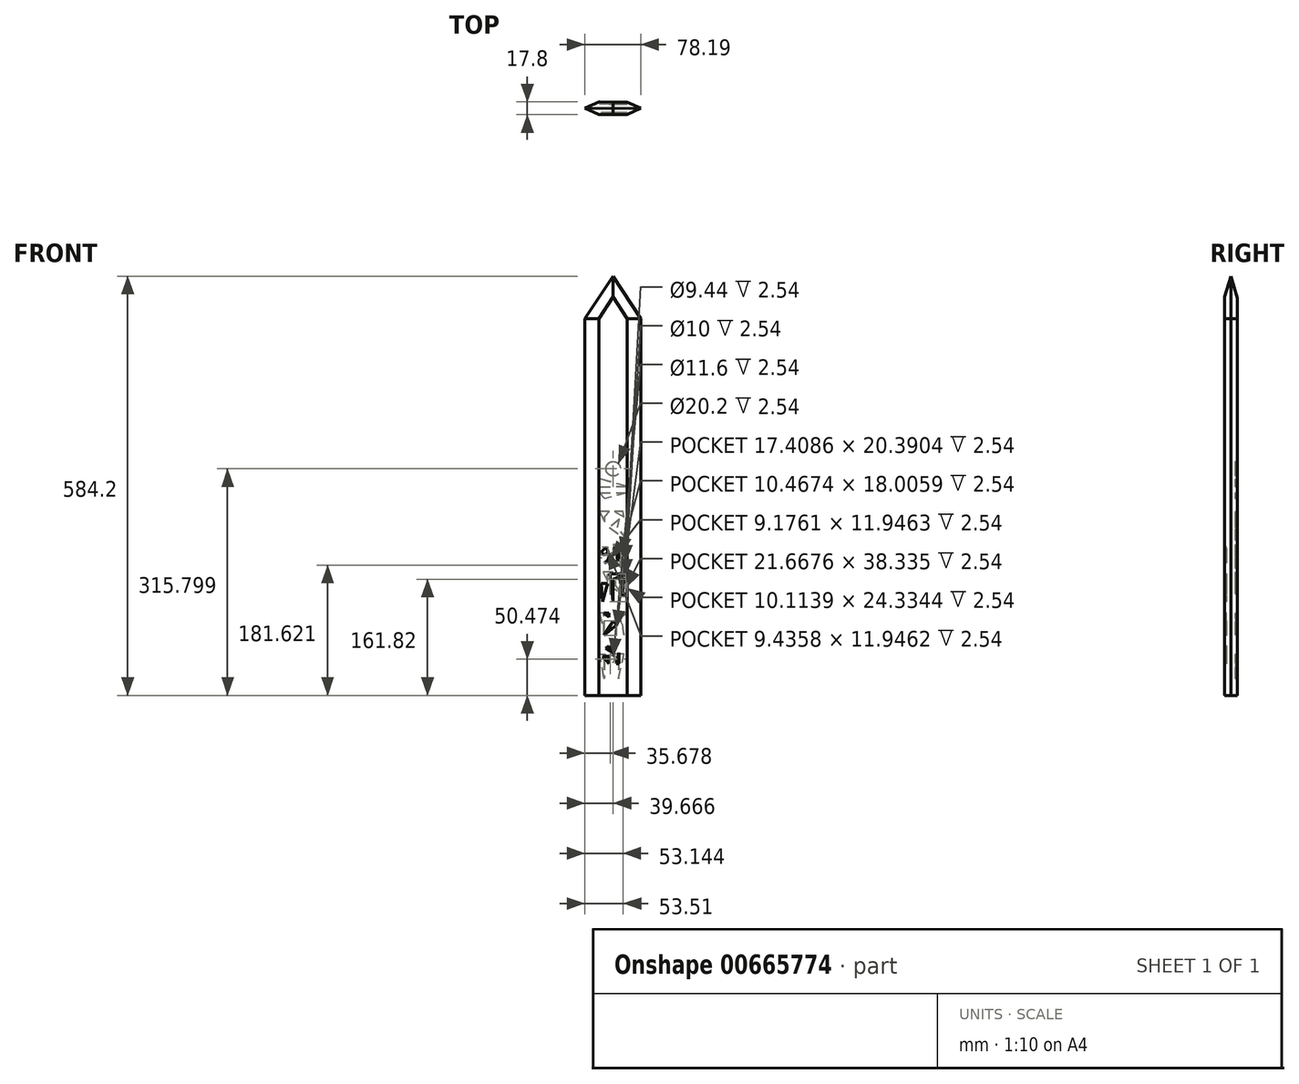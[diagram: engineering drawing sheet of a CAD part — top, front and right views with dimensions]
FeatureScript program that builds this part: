
annotation { "Feature Type Name" : "Feature", "Feature Type Description" : "" }
export const myFeature = defineFeature(function(context is Context, id is Id, definition is map)
    precondition{}
    {
        {
            var Q0;
            Q0=qCreatedBy(makeId("Top.planeOp"),FACE);
            var sketch = newSketch(context, id + "F0", { "sketchPlane" : qUnion([Q0])});
            skLineSegment(sketch, "E0.bottom", {"start": v(-40.34, -18.56) * mm, "end": v(39.23, -18.56) * mm});
            skLineSegment(sketch, "E0.top", {"start": v(-40.34, 17.67) * mm, "end": v(39.23, 17.67) * mm});
            skLineSegment(sketch, "E0.left", {"start": v(-40.34, -18.56) * mm, "end": v(-40.34, 17.67) * mm});
            skLineSegment(sketch, "E0.right", {"start": v(39.23, -18.56) * mm, "end": v(39.23, 17.67) * mm});
            skSolve(sketch);
        }
        {
            var Q0;
            Q0=makeQuery(id+"F0.imprint","IMPRINT",FACE,{"disambiguationData":[TD([[makeQuery(id+"F0.imprint","IMPRINT",EDGE,{"derivedFrom":sQuery(id+"F0.wireOp",EDGE,"E0.bottom")}),1.0]])]});
            extrude(context, id + "F1", {"entities" : qUnion([Q0]), "depth" : 12.7 * mm, "offsetDistance" : 25.4 * mm});
        }
        {
            var Q0;
            Q0=makeQuery(id+"F1.opExtrude","CAP_FACE",FACE,{"disambiguationData":[OSD([sQuery(id+"F0.wireOp",EDGE,"E0.bottom"),sQuery(id+"F0.wireOp",EDGE,"E0.top"),sQuery(id+"F0.wireOp",EDGE,"E0.left"),sQuery(id+"F0.wireOp",EDGE,"E0.right")])],"isStart":true});
            extrude(context, id + "F2", {"entities" : qUnion([Q0]), "operationType" : NewBodyOperationType.ADD, "depth" : 12.7 * mm, "offsetDistance" : 25.4 * mm});
        }
        {
            var Q0;
            Q0=makeQuery(id+"F1.opExtrude","CAP_FACE",FACE,{"disambiguationData":[OSD([sQuery(id+"F0.wireOp",EDGE,"E0.bottom"),sQuery(id+"F0.wireOp",EDGE,"E0.top"),sQuery(id+"F0.wireOp",EDGE,"E0.left"),sQuery(id+"F0.wireOp",EDGE,"E0.right")])],"isStart":false});
            var sketch = newSketch(context, id + "F3", { "sketchPlane" : qUnion([Q0])});
            skLineSegment(sketch, "E1", {"start": v(0, -17.92) * mm, "end": v(-39.6, 0) * mm});
            skLineSegment(sketch, "E2", {"start": v(0, -17.92) * mm, "end": v(38.59, 0) * mm});
            skLineSegment(sketch, "E3", {"start": v(38.59, 0) * mm, "end": v(0, 17) * mm});
            skLineSegment(sketch, "E4", {"start": v(-39.6, 0) * mm, "end": v(0, 17) * mm});
            skSolve(sketch);
        }
        {
            var Q0;
            Q0=qSketchRegion(id+"F3",true);
            extrude(context, id + "F4", {"entities" : qUnion([Q0]), "operationType" : NewBodyOperationType.ADD, "depth" : 508 * mm, "offsetDistance" : 25.4 * mm});
        }
        {
            var Q0;
            Q0=makeQuery(id+"F4.opExtrude","CAP_FACE",FACE,{"disambiguationData":[OSD([sQuery(id+"F3.wireOp",EDGE,"E1"),sQuery(id+"F3.wireOp",EDGE,"E2"),sQuery(id+"F3.wireOp",EDGE,"E3"),sQuery(id+"F3.wireOp",EDGE,"E4")])],"isStart":false});
            var sketch = newSketch(context, id + "F5", { "sketchPlane" : qUnion([Q0])});
            skSolve(sketch);
        }
        {
            var Q0;
            Q0=makeQuery(id+"F5.imprint","IMPRINT",FACE,{"disambiguationData":[TD([[makeQuery(id+"F5.imprint","IMPRINT",EDGE,{"derivedFrom":makeQuery(id+"F4.opExtrude","CAP_EDGE",EDGE,{"disambiguationData":[OSD([sQuery(id+"F3.wireOp",EDGE,"E1")])],"isStart":false})}),-1.0]])]});
            var sketch = newSketch(context, id + "F6", { "sketchPlane" : qUnion([Q0])});
            skSolve(sketch);
        }
        {
            var Q0;
            Q0=qSketchRegion(id+"F6",true);
            var Q1;
            Q1=makeQuery(id+"F5.imprint","IMPRINT",FACE,{"disambiguationData":[TD([[makeQuery(id+"F5.imprint","IMPRINT",EDGE,{"derivedFrom":makeQuery(id+"F4.opExtrude","CAP_EDGE",EDGE,{"disambiguationData":[OSD([sQuery(id+"F3.wireOp",EDGE,"E1")])],"isStart":false})}),-1.0]])]});
            extrude(context, id + "F7", {"entities" : qUnion([Q0, Q1]), "operationType" : NewBodyOperationType.ADD, "depth" : 76.2 * mm, "offsetDistance" : 25.4 * mm});
        }
        {
            var Q0;
            Q0=makeQuery(id+"F7.opExtrude","CAP_FACE",FACE,{"disambiguationData":[OSD([sQuery(id+"F3.wireOp",EDGE,"E1"),sQuery(id+"F3.wireOp",EDGE,"E2"),sQuery(id+"F3.wireOp",EDGE,"E3"),sQuery(id+"F3.wireOp",EDGE,"E4")])],"isStart":false});
            chamfer(context, id + "F8", {"entities" : qUnion([Q0]), "chamferType" : ChamferType.OFFSET_ANGLE, "width" : 59.46 * mm, "oppositeDirection" : false, "angle" : 15 * degree, "tangentPropagation" : true});
        }
        {
            var Q0;
            {var subQ0=sQuery(id+"F0.wireOp",EDGE,"E0.top");Q0=makeQuery(id+"F2.boolean.opBoolean","MERGE",FACE,{"derivedFrom":[makeQuery(id+"F1.opExtrude","SWEPT_FACE",FACE,{"disambiguationData":[OSD([subQ0])]}),makeQuery(id+"F2.opExtrude","SWEPT_FACE",FACE,{"disambiguationData":[OSD([subQ0])]})]});}
            extrude(context, id + "F9", {"entities" : qUnion([Q0]), "operationType" : NewBodyOperationType.REMOVE, "oppositeDirection" : true, "depth" : 25.4 * mm, "offsetDistance" : 25.4 * mm});
        }
        {
            var Q0;
            {var subQ0=sQuery(id+"F0.wireOp",EDGE,"E0.bottom");Q0=makeQuery(id+"F2.boolean.opBoolean","MERGE",FACE,{"derivedFrom":[makeQuery(id+"F1.opExtrude","SWEPT_FACE",FACE,{"disambiguationData":[OSD([subQ0])]}),makeQuery(id+"F2.opExtrude","SWEPT_FACE",FACE,{"disambiguationData":[OSD([subQ0])]})]});}
            extrude(context, id + "F10", {"entities" : qUnion([Q0]), "operationType" : NewBodyOperationType.REMOVE, "oppositeDirection" : true, "depth" : 25.4 * mm, "offsetDistance" : 25.4 * mm});
        }
        {
            var Q0;
            {var subQ0=sQuery(id+"F0.wireOp",EDGE,"E0.bottom");var subQ1=sQuery(id+"F0.wireOp",EDGE,"E0.top");Q0=makeQuery(id+"F10.boolean.opBoolean","MERGE",FACE,{"derivedFrom":[makeQuery(id+"F9.boolean.opBoolean","COPY",FACE,{"derivedFrom":makeQuery(id+"F9.opExtrude","SWEPT_FACE",FACE,{"disambiguationData":[OSD([subQ1]),TDD([makeQuery(id+"F1.opExtrude","CAP_EDGE",EDGE,{"disambiguationData":[OSD([subQ1])],"isStart":false})])]})}),makeQuery(id+"F10.opExtrude","SWEPT_FACE",FACE,{"disambiguationData":[OSD([subQ0]),TDD([makeQuery(id+"F1.opExtrude","CAP_EDGE",EDGE,{"disambiguationData":[OSD([subQ0])],"isStart":false})])]})]});}
            var sketch = newSketch(context, id + "F11", { "sketchPlane" : qUnion([Q0])});
            skLineSegment(sketch, "E5", {"start": v(-19.8, 8.96) * mm, "end": v(19.3, 8.96) * mm});
            skLineSegment(sketch, "E6", {"start": v(19.3, -8.5) * mm, "end": v(-19, -8.84) * mm});
            skSolve(sketch);
        }
        {
            var Q0;
            {var subQ0=sQuery(id+"F11.wireOp",EDGE,"E6");Q0=makeQuery(id+"F11.imprint","IMPRINT",FACE,{"disambiguationData":[TD([[makeQuery(id+"F11.imprint","IMPRINT",EDGE,{"derivedFrom":subQ0}),1.0]])]});}
            var Q1;
            {var subQ0=sQuery(id+"F11.wireOp",EDGE,"E5");Q1=makeQuery(id+"F11.imprint","IMPRINT",FACE,{"disambiguationData":[TD([[makeQuery(id+"F11.imprint","IMPRINT",EDGE,{"derivedFrom":subQ0}),1.0]])]});}
            extrude(context, id + "F12", {"entities" : qUnion([Q0, Q1]), "operationType" : NewBodyOperationType.REMOVE, "oppositeDirection" : true, "depth" : 990.6 * mm, "offsetDistance" : 25.4 * mm});
        }
        {
            var Q0;
            Q0=makeQuery(id+"F12.boolean.opBoolean","COPY",FACE,{"derivedFrom":makeQuery(id+"F12.opExtrude","SWEPT_FACE",FACE,{"disambiguationData":[OSD([sQuery(id+"F11.wireOp",EDGE,"E5")])]})});
            var sketch = newSketch(context, id + "F13", { "sketchPlane" : qUnion([Q0])});
            skLineSegment(sketch, "E7", {"start": v(-14.74, 67.28) * mm, "end": v(-5.7, 67.28) * mm});
            skLineSegment(sketch, "E8", {"start": v(-5.7, 67.28) * mm, "end": v(-5.7, 56.81) * mm});
            skLineSegment(sketch, "E9", {"start": v(-14.94, 75.78) * mm, "end": v(-5.7, 81.54) * mm});
            skLineSegment(sketch, "E10", {"start": v(-5.7, 81.54) * mm, "end": v(0, 72.4) * mm});
            skLineSegment(sketch, "E11", {"start": v(0, 56.81) * mm, "end": v(8.25, 56.81) * mm});
            skLineSegment(sketch, "E12", {"start": v(8.25, 56.81) * mm, "end": v(8.25, 72.4) * mm});
            skLineSegment(sketch, "E13", {"start": v(-10.33, 78.66) * mm, "end": v(0, 72.4) * mm});
            skLineSegment(sketch, "E14", {"start": v(-14.94, 75.78) * mm, "end": v(-5.7, 72.4) * mm});
            skLineSegment(sketch, "E15", {"start": v(8.25, 72.4) * mm, "end": v(4.12, 56.81) * mm});
            skLineSegment(sketch, "E16", {"start": v(4.12, 56.81) * mm, "end": v(0, 56.81) * mm});
            skLineSegment(sketch, "E17", {"start": v(-14.74, 67.28) * mm, "end": v(-5.7, 56.81) * mm});
            skLineSegment(sketch, "E18", {"start": v(0, 116.5) * mm, "end": v(4.63, 111.15) * mm});
            skLineSegment(sketch, "E19", {"start": v(4.63, 111.15) * mm, "end": v(0, 107.16) * mm});
            skLineSegment(sketch, "E20", {"start": v(0, 107.16) * mm, "end": v(-3.45, 111.15) * mm});
            skLineSegment(sketch, "E21", {"start": v(-3.45, 111.15) * mm, "end": v(0, 116.5) * mm});
            skLineSegment(sketch, "E22", {"start": v(0, 107.16) * mm, "end": v(-12.78, 96.12) * mm});
            skLineSegment(sketch, "E23", {"start": v(-3.45, 111.15) * mm, "end": v(-12.78, 96.12) * mm});
            skLineSegment(sketch, "E24", {"start": v(4.63, 127.22) * mm, "end": v(12.87, 127.22) * mm});
            skLineSegment(sketch, "E25", {"start": v(12.87, 127.22) * mm, "end": v(7.92, 116.5) * mm});
            skLineSegment(sketch, "E26", {"start": v(7.92, 116.5) * mm, "end": v(4.63, 127.22) * mm});
            skLineSegment(sketch, "E27", {"start": v(-12.78, 127.22) * mm, "end": v(-5.7, 127.22) * mm});
            skLineSegment(sketch, "E28", {"start": v(-5.7, 127.22) * mm, "end": v(-5.7, 121.45) * mm});
            skLineSegment(sketch, "E29", {"start": v(-5.7, 121.45) * mm, "end": v(-12.78, 127.22) * mm});
            skLineSegment(sketch, "E30", {"start": v(-16.76, 168.42) * mm, "end": v(-7.82, 168.42) * mm});
            skLineSegment(sketch, "E31", {"start": v(-7.82, 169.42) * mm, "end": v(-15.11, 143.42) * mm});
            skLineSegment(sketch, "E32", {"start": v(-15.11, 143.42) * mm, "end": v(-16.76, 168.42) * mm});
            skLineSegment(sketch, "E33", {"start": v(-4.33, 181.75) * mm, "end": v(17.33, 181.75) * mm});
            skLineSegment(sketch, "E34", {"start": v(17.33, 181.75) * mm, "end": v(0, 174.42) * mm});
            skLineSegment(sketch, "E35", {"start": v(0, 174.42) * mm, "end": v(0, 143.42) * mm});
            skLineSegment(sketch, "E36", {"start": v(0, 143.42) * mm, "end": v(-4.33, 181.75) * mm});
            skLineSegment(sketch, "E37", {"start": v(9.18, 174.42) * mm, "end": v(19.3, 174.42) * mm});
            skLineSegment(sketch, "E38", {"start": v(19.3, 174.42) * mm, "end": v(13.51, 168.42) * mm});
            skLineSegment(sketch, "E39", {"start": v(13.51, 168.42) * mm, "end": v(13.51, 150.09) * mm});
            skLineSegment(sketch, "E40", {"start": v(13.51, 150.09) * mm, "end": v(9.18, 174.42) * mm});
            skLineSegment(sketch, "E41", {"start": v(-16.43, 212.64) * mm, "end": v(-11.58, 207.8) * mm});
            skLineSegment(sketch, "E42", {"start": v(-11.58, 207.8) * mm, "end": v(-6.99, 212.38) * mm});
            skLineSegment(sketch, "E43", {"start": v(-6.99, 212.38) * mm, "end": v(-10.02, 219.74) * mm});
            skLineSegment(sketch, "E44", {"start": v(-16.43, 212.64) * mm, "end": v(-10.02, 219.74) * mm});
            skLineSegment(sketch, "E45", {"start": v(-4.48, 209.35) * mm, "end": v(-7.08, 201.56) * mm});
            skLineSegment(sketch, "E46", {"start": v(-4.48, 209.35) * mm, "end": v(-3.1, 200.7) * mm});
            skLineSegment(sketch, "E47", {"start": v(-3.1, 200.7) * mm, "end": v(-12.27, 197.4) * mm});
            skLineSegment(sketch, "E48", {"start": v(-12.27, 197.4) * mm, "end": v(-7.08, 201.56) * mm});
            skLineSegment(sketch, "E49", {"start": v(0, 217.32) * mm, "end": v(10.58, 217.32) * mm});
            skLineSegment(sketch, "E50", {"start": v(10.58, 217.84) * mm, "end": v(6.43, 199.3) * mm});
            skLineSegment(sketch, "E51", {"start": v(6.43, 199.3) * mm, "end": v(4.7, 213.85) * mm});
            skLineSegment(sketch, "E52", {"start": v(4.7, 213.85) * mm, "end": v(0, 217.32) * mm});
            skSolve(sketch);
        }
        {
            var Q0;
            Q0 = qSketchRegion(id + "F13", true);
            extrude(context, id + "F14", {"entities" : qUnion([Q0]), "operationType" : NewBodyOperationType.REMOVE, "oppositeDirection" : true, "depth" : 2.54 * mm, "offsetDistance" : 25.4 * mm});
        }
        {
            var Q0;
            Q0=makeQuery(id+"F12.boolean.opBoolean","COPY",FACE,{"derivedFrom":makeQuery(id+"F12.opExtrude","SWEPT_FACE",FACE,{"disambiguationData":[OSD([sQuery(id+"F11.wireOp",EDGE,"E6")])]})});
            var sketch = newSketch(context, id + "F15", { "sketchPlane" : qUnion([Q0])});
            skLineSegment(sketch, "E53", {"start": v(-14.88, 70.26) * mm, "end": v(0, 70.26) * mm});
            skLineSegment(sketch, "E54", {"start": v(0, 70.26) * mm, "end": v(-7.44, 63.17) * mm});
            skPoint(sketch, "E54.endSnap0", {"position": v(-7.44, 70.26) * mm});
            skLineSegment(sketch, "E55", {"start": v(-7.44, 63.17) * mm, "end": v(-7.44, 35.84) * mm});
            skLineSegment(sketch, "E56", {"start": v(-7.44, 35.84) * mm, "end": v(-14.88, 70.26) * mm});
            skLineSegment(sketch, "E57", {"start": v(19.08, 70.26) * mm, "end": v(11.13, 70.26) * mm});
            skLineSegment(sketch, "E58", {"start": v(11.13, 70.26) * mm, "end": v(12.66, 63.17) * mm});
            skLineSegment(sketch, "E59", {"start": v(12.66, 63.17) * mm, "end": v(12.66, 36.86) * mm});
            skLineSegment(sketch, "E60", {"start": v(12.66, 36.86) * mm, "end": v(19.08, 70.26) * mm});
            skCircle(sketch, "E61", {"center": v(3.99, 63.17) * mm, "radius": 5.8 * mm});
            skLineSegment(sketch, "E62", {"start": v(-19.22, 127.45) * mm, "end": v(-7.74, 127.45) * mm});
            skLineSegment(sketch, "E63", {"start": v(-7.74, 127.45) * mm, "end": v(-14.88, 97.08) * mm});
            skLineSegment(sketch, "E64", {"start": v(-14.88, 97.08) * mm, "end": v(-11.3, 122.4) * mm});
            skPoint(sketch, "E64.endSnap0", {"position": v(-11.3, 112.27) * mm});
            skLineSegment(sketch, "E65", {"start": v(-11.3, 122.4) * mm, "end": v(-19.22, 127.45) * mm});
            skLineSegment(sketch, "E66", {"start": v(0, 122.4) * mm, "end": v(4.4, 121.77) * mm});
            skLineSegment(sketch, "E67", {"start": v(4.4, 121.77) * mm, "end": v(4.4, 112.27) * mm});
            skLineSegment(sketch, "E68", {"start": v(4.4, 112.27) * mm, "end": v(4.4, 121.77) * mm});
            skLineSegment(sketch, "E69", {"start": v(0, 122.4) * mm, "end": v(4.4, 112.27) * mm});
            skLineSegment(sketch, "E70", {"start": v(12.66, 127.45) * mm, "end": v(19.08, 127.45) * mm});
            skLineSegment(sketch, "E71", {"start": v(19.08, 127.45) * mm, "end": v(12.66, 100.12) * mm});
            skLineSegment(sketch, "E72", {"start": v(12.66, 100.12) * mm, "end": v(12.66, 127.45) * mm});
            skCircle(sketch, "E73", {"center": v(-13.48, 174.52) * mm, "radius": 5 * mm});
            skPoint(sketch, "E73.centerSnap0", {"position": v(-13.48, 127.45) * mm});
            skLineSegment(sketch, "E74", {"start": v(-3.53, 171.7) * mm, "end": v(6.42, 166.76) * mm});
            skLineSegment(sketch, "E75", {"start": v(6.42, 166.76) * mm, "end": v(-12.78, 154.05) * mm});
            skLineSegment(sketch, "E76", {"start": v(-12.78, 154.05) * mm, "end": v(-3.53, 165.34) * mm});
            skLineSegment(sketch, "E77", {"start": v(-3.53, 165.34) * mm, "end": v(-3.53, 171.7) * mm});
            skLineSegment(sketch, "E78", {"start": v(0, 184.4) * mm, "end": v(14.24, 184.4) * mm});
            skLineSegment(sketch, "E79", {"start": v(14.24, 184.4) * mm, "end": v(7.94, 171.7) * mm});
            skLineSegment(sketch, "E80", {"start": v(7.94, 171.7) * mm, "end": v(7.94, 181.23) * mm});
            skLineSegment(sketch, "E81", {"start": v(7.94, 181.23) * mm, "end": v(0, 184.4) * mm});
            skCircle(sketch, "E82", {"center": v(-13.84, 194.32) * mm, "radius": 4.72 * mm});
            skLineSegment(sketch, "E83", {"start": v(5.32, 206.09) * mm, "end": v(0, 211.72) * mm});
            skLineSegment(sketch, "E84", {"start": v(0, 211.72) * mm, "end": v(19.08, 204.87) * mm});
            skLineSegment(sketch, "E85", {"start": v(-14.53, 222.82) * mm, "end": v(0, 222.82) * mm});
            skLineSegment(sketch, "E86", {"start": v(0, 222.82) * mm, "end": v(-9.95, 208.33) * mm});
            skLineSegment(sketch, "E87", {"start": v(-9.95, 208.33) * mm, "end": v(-9.95, 216.86) * mm});
            skLineSegment(sketch, "E88", {"start": v(-9.95, 216.86) * mm, "end": v(-14.53, 222.82) * mm});
            skLineSegment(sketch, "E89", {"start": v(5.32, 206.09) * mm, "end": v(-5.01, 193.84) * mm});
            skLineSegment(sketch, "E90", {"start": v(-5.01, 193.84) * mm, "end": v(18.42, 205.1) * mm});
            skLineSegment(sketch, "E91", {"start": v(-8.92, 258.02) * mm, "end": v(5.55, 246.8) * mm});
            skLineSegment(sketch, "E92", {"start": v(5.55, 246.8) * mm, "end": v(-19.22, 229.3) * mm});
            skLineSegment(sketch, "E93", {"start": v(-19.22, 229.3) * mm, "end": v(-6.2, 246.8) * mm});
            skLineSegment(sketch, "E94", {"start": v(-6.2, 246.8) * mm, "end": v(-8.92, 258.02) * mm});
            skLineSegment(sketch, "E95", {"start": v(5.55, 268.8) * mm, "end": v(19.08, 268.8) * mm});
            skLineSegment(sketch, "E96", {"start": v(19.08, 268.8) * mm, "end": v(11.43, 254.43) * mm});
            skLineSegment(sketch, "E97", {"start": v(11.43, 254.43) * mm, "end": v(11.43, 262.06) * mm});
            skLineSegment(sketch, "E98", {"start": v(11.43, 262.06) * mm, "end": v(5.55, 268.8) * mm});
            skLineSegment(sketch, "E99", {"start": v(-13.44, 268.8) * mm, "end": v(-1.68, 268.8) * mm});
            skPoint(sketch, "E99.endSnap0", {"position": v(-1.68, 252.41) * mm});
            skLineSegment(sketch, "E100", {"start": v(-1.68, 268.8) * mm, "end": v(-14.8, 261.61) * mm});
            skLineSegment(sketch, "E101", {"start": v(-14.8, 261.61) * mm, "end": v(-13.44, 268.8) * mm});
            skLineSegment(sketch, "E102", {"start": v(11.43, 286.8) * mm, "end": v(19.08, 295) * mm});
            skLineSegment(sketch, "E103", {"start": v(19.08, 295) * mm, "end": v(-19.22, 295) * mm});
            skLineSegment(sketch, "E104", {"start": v(-19.22, 295) * mm, "end": v(11.43, 286.8) * mm});
            skLineSegment(sketch, "E105", {"start": v(-19.22, 303.93) * mm, "end": v(19.08, 314.35) * mm});
            skLineSegment(sketch, "E106", {"start": v(19.08, 314.35) * mm, "end": v(19.08, 303.18) * mm});
            skLineSegment(sketch, "E107", {"start": v(19.08, 303.18) * mm, "end": v(-19.22, 303.93) * mm});
            skCircle(sketch, "E108", {"center": v(0, 328.5) * mm, "radius": 10.1 * mm});
            skSolve(sketch);
        }
        {
            var Q0;
            {var subQ0=sQuery(id+"F15.wireOp",EDGE,"E83");Q0=makeQuery(id+"F15.imprint","IMPRINT",FACE,{"disambiguationData":[TD([[makeQuery(id+"F15.imprint","IMPRINT",EDGE,{"derivedFrom":subQ0}),-1.0]])]});}
            var Q1;
            Q1=makeQuery(id+"F15.imprint","IMPRINT",FACE,{"disambiguationData":[TD([[makeQuery(id+"F15.imprint","IMPRINT",EDGE,{"derivedFrom":sQuery(id+"F15.wireOp",EDGE,"E82")}),1.0]])]});
            var Q2;
            Q2=makeQuery(id+"F15.imprint","IMPRINT",FACE,{"disambiguationData":[TD([[makeQuery(id+"F15.imprint","IMPRINT",EDGE,{"derivedFrom":sQuery(id+"F15.wireOp",EDGE,"E85")}),-1.0]])]});
            var Q3;
            Q3=makeQuery(id+"F15.imprint","IMPRINT",FACE,{"disambiguationData":[TD([[makeQuery(id+"F15.imprint","IMPRINT",EDGE,{"derivedFrom":sQuery(id+"F15.wireOp",EDGE,"E78")}),-1.0]])]});
            var Q4;
            Q4=makeQuery(id+"F15.imprint","IMPRINT",FACE,{"disambiguationData":[TD([[makeQuery(id+"F15.imprint","IMPRINT",EDGE,{"derivedFrom":sQuery(id+"F15.wireOp",EDGE,"E74")}),-1.0]])]});
            var Q5;
            Q5=makeQuery(id+"F15.imprint","IMPRINT",FACE,{"disambiguationData":[TD([[makeQuery(id+"F15.imprint","IMPRINT",EDGE,{"derivedFrom":sQuery(id+"F15.wireOp",EDGE,"E73")}),1.0]])]});
            var Q6;
            Q6=makeQuery(id+"F15.imprint","IMPRINT",FACE,{"disambiguationData":[TD([[makeQuery(id+"F15.imprint","IMPRINT",EDGE,{"derivedFrom":sQuery(id+"F15.wireOp",EDGE,"E62")}),-1.0]])]});
            var Q7;
            Q7=makeQuery(id+"F15.imprint","IMPRINT",FACE,{"disambiguationData":[TD([[makeQuery(id+"F15.imprint","IMPRINT",EDGE,{"derivedFrom":sQuery(id+"F15.wireOp",EDGE,"E68")}),1.0]])]});
            var Q8;
            Q8=makeQuery(id+"F15.imprint","IMPRINT",FACE,{"disambiguationData":[TD([[makeQuery(id+"F15.imprint","IMPRINT",EDGE,{"derivedFrom":sQuery(id+"F15.wireOp",EDGE,"E70")}),-1.0]])]});
            var Q9;
            Q9=makeQuery(id+"F15.imprint","IMPRINT",FACE,{"disambiguationData":[TD([[makeQuery(id+"F15.imprint","IMPRINT",EDGE,{"derivedFrom":sQuery(id+"F15.wireOp",EDGE,"E61")}),1.0]])]});
            var Q10;
            Q10=makeQuery(id+"F15.imprint","IMPRINT",FACE,{"disambiguationData":[TD([[makeQuery(id+"F15.imprint","IMPRINT",EDGE,{"derivedFrom":sQuery(id+"F15.wireOp",EDGE,"E57")}),1.0]])]});
            var Q11;
            Q11=makeQuery(id+"F15.imprint","IMPRINT",FACE,{"disambiguationData":[TD([[makeQuery(id+"F15.imprint","IMPRINT",EDGE,{"derivedFrom":sQuery(id+"F15.wireOp",EDGE,"E53")}),-1.0]])]});
            extrude(context, id + "F16", {"entities" : qUnion([Q0, Q1, Q2, Q3, Q4, Q5, Q6, Q7, Q8, Q9, Q10, Q11]), "operationType" : NewBodyOperationType.REMOVE, "oppositeDirection" : true, "depth" : 2.54 * mm, "offsetDistance" : 25.4 * mm});
        }
        {
            var Q0;
            Q0=makeQuery(id+"F15.imprint","IMPRINT",FACE,{"disambiguationData":[TD([[makeQuery(id+"F15.imprint","IMPRINT",EDGE,{"derivedFrom":sQuery(id+"F15.wireOp",EDGE,"E99")}),-1.0]])]});
            var Q1;
            Q1=makeQuery(id+"F15.imprint","IMPRINT",FACE,{"disambiguationData":[TD([[makeQuery(id+"F15.imprint","IMPRINT",EDGE,{"derivedFrom":sQuery(id+"F15.wireOp",EDGE,"E91")}),-1.0]])]});
            var Q2;
            Q2=makeQuery(id+"F15.imprint","IMPRINT",FACE,{"disambiguationData":[TD([[makeQuery(id+"F15.imprint","IMPRINT",EDGE,{"derivedFrom":sQuery(id+"F15.wireOp",EDGE,"E95")}),-1.0]])]});
            extrude(context, id + "F17", {"entities" : qUnion([Q0, Q1, Q2]), "operationType" : NewBodyOperationType.REMOVE, "oppositeDirection" : true, "depth" : 2.54 * mm, "offsetDistance" : 25.4 * mm});
        }
        {
            var Q0;
            Q0=makeQuery(id+"F15.imprint","IMPRINT",FACE,{"disambiguationData":[TD([[makeQuery(id+"F15.imprint","IMPRINT",EDGE,{"derivedFrom":sQuery(id+"F15.wireOp",EDGE,"E108")}),1.0]])]});
            var Q1;
            Q1=makeQuery(id+"F15.imprint","IMPRINT",FACE,{"disambiguationData":[TD([[makeQuery(id+"F15.imprint","IMPRINT",EDGE,{"derivedFrom":sQuery(id+"F15.wireOp",EDGE,"E105")}),-1.0]])]});
            var Q2;
            Q2=makeQuery(id+"F15.imprint","IMPRINT",FACE,{"disambiguationData":[TD([[makeQuery(id+"F15.imprint","IMPRINT",EDGE,{"derivedFrom":sQuery(id+"F15.wireOp",EDGE,"E102")}),1.0]])]});
            extrude(context, id + "F18", {"entities" : qUnion([Q0, Q1, Q2]), "operationType" : NewBodyOperationType.REMOVE, "oppositeDirection" : true, "depth" : 2.54 * mm, "offsetDistance" : 25.4 * mm});
        }
    });
